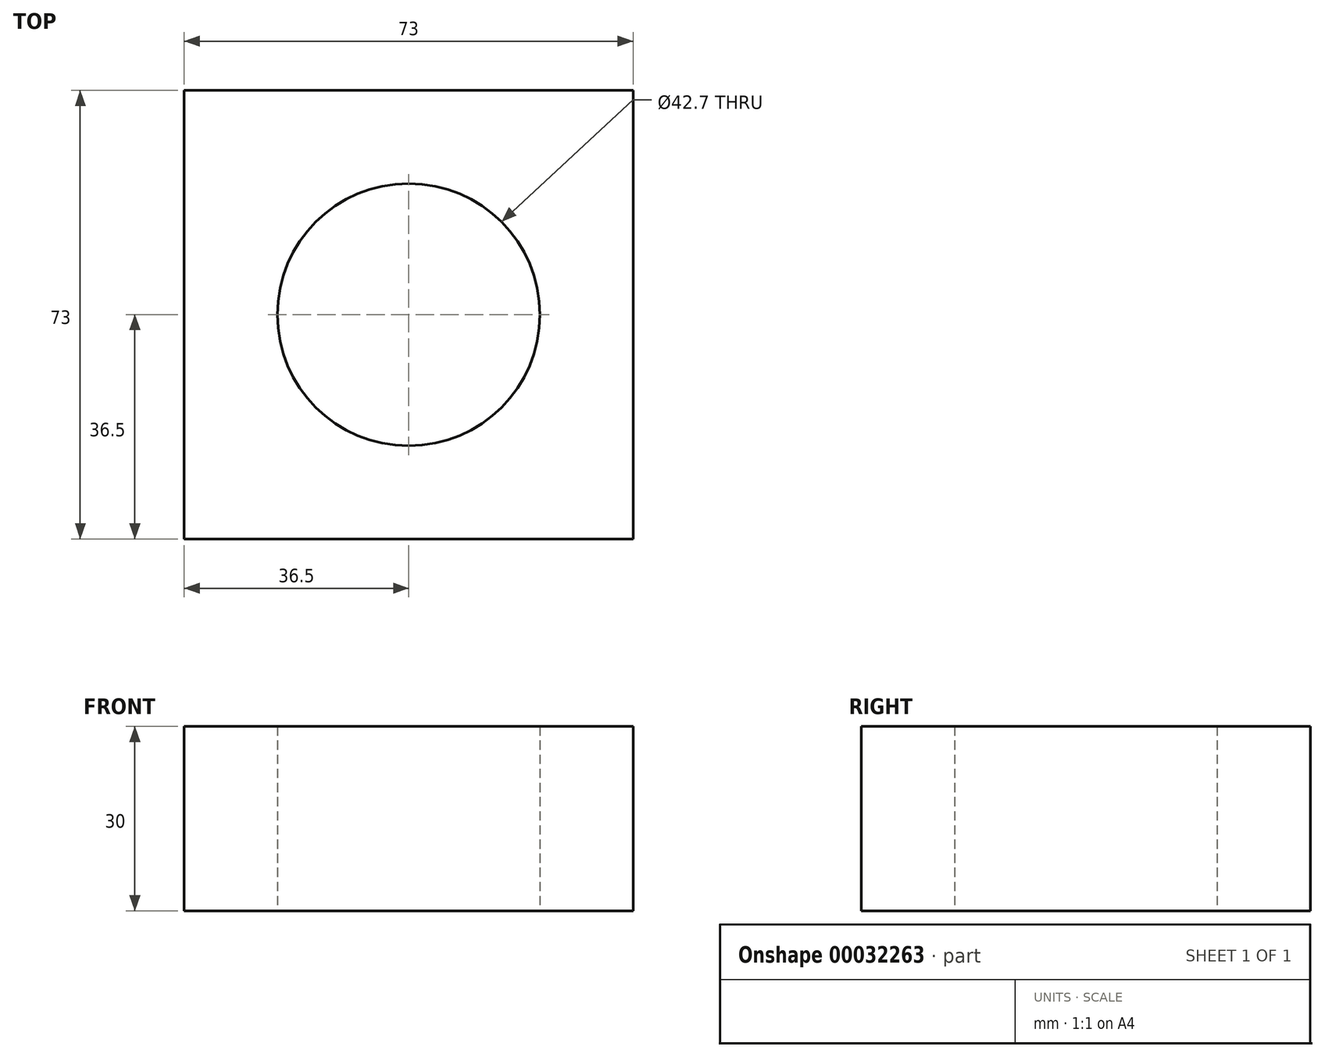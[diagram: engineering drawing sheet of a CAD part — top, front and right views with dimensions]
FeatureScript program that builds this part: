
annotation { "Feature Type Name" : "Feature", "Feature Type Description" : "" }
export const myFeature = defineFeature(function(context is Context, id is Id, definition is map)
    precondition{}
    {
        {
            var Q0;
            Q0=qCreatedBy(makeId("Top.planeOp"),FACE);
            var sketch = newSketch(context, id + "F0", { "sketchPlane" : qUnion([Q0])});
            skLineSegment(sketch, "E0.rect.bottom", {"start": v(-36.5, 36.5) * mm, "end": v(36.5, 36.5) * mm});
            skLineSegment(sketch, "E0.rect.top", {"start": v(-36.5, -36.5) * mm, "end": v(36.5, -36.5) * mm});
            skLineSegment(sketch, "E0.rect.left", {"start": v(-36.5, 36.5) * mm, "end": v(-36.5, -36.5) * mm});
            skLineSegment(sketch, "E0.rect.right", {"start": v(36.5, 36.5) * mm, "end": v(36.5, -36.5) * mm});
            skPoint(sketch, "E0.rect.middle", {"position": v(0, 0) * mm});
            skCircle(sketch, "E1", {"center": v(0, 0) * mm, "radius": 21.35 * mm});
            skSolve(sketch);
        }
        {
            var Q0;
            Q0=makeQuery(id+"F0.imprint","IMPRINT",FACE,{"disambiguationData":[TD([[makeQuery(id+"F0.imprint","IMPRINT",EDGE,{"derivedFrom":sQuery(id+"F0.wireOp",EDGE,"E0.rect.bottom")}),-1.0]])]});
            extrude(context, id + "F1", {"entities" : qUnion([Q0]), "depth" : 30 * mm});
        }
    });
